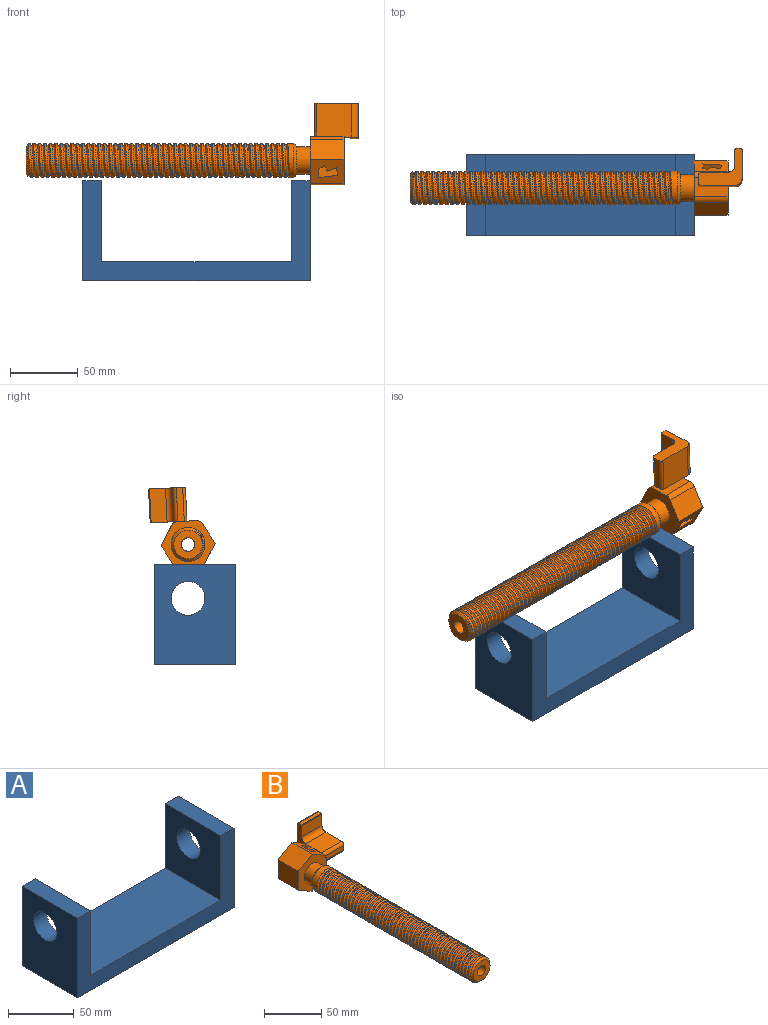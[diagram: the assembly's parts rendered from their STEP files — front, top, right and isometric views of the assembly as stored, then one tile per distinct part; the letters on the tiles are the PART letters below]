
ASSEMBLY  parts=2 mates=1
PART A: 12 faces, bbox 168x60x74 mm
  f0: plane 74x60mm, normal (-1,0,0), area 3949.1mm2, adj f1,f7,f8,f9,f10
  f1: plane 168x60mm, normal (0,0,-1), area 10080mm2, adj f0,f2,f8,f9
  f2: plane 74x60mm, normal (1,0,0), area 3949.1mm2, adj f1,f3,f8,f9,f11
  f3: plane 60x14mm, normal (0,0,1), area 840mm2, adj f2,f4,f8,f9
  f4: plane 60x60mm, normal (-1,0,0), area 3109.1mm2, adj f3,f5,f8,f9,f11
  f5: plane 140x60mm, normal (0,0,1), area 8400mm2, adj f4,f6,f8,f9
  f6: plane 60x60mm, normal (1,0,0), area 3109.1mm2, adj f5,f7,f8,f9,f10
  f7: plane 60x14mm, normal (0,0,1), area 840mm2, adj f0,f6,f8,f9
  f8: plane 168x74mm, normal (0,-1,0), area 4032mm2, adj f0,f1,f2,f3,f4,f5,f6,f7
  f9: plane 168x74mm, normal (0,1,0), area 4032mm2, adj f0,f1,f2,f3,f4,f5,f6,f7
  f10: cylinder r=12.5mm len=25mm, axis (1,0,0), area 1099.6mm2, adj f0,f6
  f11: cylinder r=12.5mm len=25mm, axis (1,0,0), area 1099.6mm2, adj f2,f4
PART B: 91 faces, bbox 60.5x247.5x48.1 mm
  f0: plane 25x14.23mm, normal (1,0,0), area 200.3mm2, adj f7,f8,f65,f66,f78,f79,f80,f81
  f1: plane 25x14.82mm, normal (0.5,0,0.87), area 340.3mm2, adj f4,f7,f8,f65,f71,f72,f73,f74
  f2: plane 25x17.32mm, normal (-0.5,0,-0.87), area 412.4mm2, adj f5,f6,f7,f8,f67,f68,f69,f70
  f3: cylinder r=5mm len=235mm, axis (0,1,0), area 7166mm2, adj f8,f58,f67,f68,f69,f70,f71,f72
  f4: plane 25x17.32mm, normal (-0.5,0,0.87), area 500mm2, adj f1,f5,f7,f8
  f5: plane 25x20mm, normal (-1,0,0), area 500mm2, adj f2,f4,f7,f8
  f6: plane 25x14.82mm, normal (0.5,0,-0.87), area 427.8mm2, adj f2,f7,f8,f66
  f7: plane 40x34.64mm, normal (0,-1,0), area 722.4mm2, adj f0,f1,f2,f4,f5,f6,f9,f65
  f8: plane 40x34.64mm, normal (0,1,0), area 958mm2, adj f0,f1,f2,f3,f4,f5,f6,f65
  f9: cylinder r=10mm len=20mm, axis (0,1,0), area 628.3mm2, adj f7,f59
  f10: cylinder r=12.5mm len=25mm, axis (0,1,0), area 462.9mm2, adj f57,f60,f62,f63,f64
  f11: cylinder r=12.5mm len=25mm, axis (0,1,0), area 100.8mm2, adj f12,f61,f63,f64
  f12: cylinder r=12.5mm len=25mm, axis (0,1,0), area 125.8mm2, adj f11,f13,f63,f64
  f13: cylinder r=12.5mm len=25mm, axis (0,1,0), area 125.7mm2, adj f12,f14,f63,f64
  f14: cylinder r=12.5mm len=25mm, axis (0,1,0), area 125.8mm2, adj f13,f15,f63,f64
  f15: cylinder r=12.5mm len=25mm, axis (0,1,0), area 125.6mm2, adj f14,f16,f63,f64
  f16: cylinder r=12.5mm len=25mm, axis (0,1,0), area 125.7mm2, adj f15,f17,f63,f64
  f17: cylinder r=12.5mm len=25mm, axis (0,1,0), area 125.7mm2, adj f16,f18,f63,f64
  f18: cylinder r=12.5mm len=25mm, axis (0,1,0), area 125.8mm2, adj f17,f19,f63,f64
  f19: cylinder r=12.5mm len=25mm, axis (0,1,0), area 125.7mm2, adj f18,f20,f63,f64
  f20: cylinder r=12.5mm len=25mm, axis (0,1,0), area 125.7mm2, adj f19,f21,f63,f64
  f21: cylinder r=12.5mm len=25mm, axis (0,1,0), area 125.7mm2, adj f20,f22,f63,f64
  f22: cylinder r=12.5mm len=25mm, axis (0,1,0), area 125.7mm2, adj f21,f23,f63,f64
  f23: cylinder r=12.5mm len=25mm, axis (0,1,0), area 125.8mm2, adj f22,f24,f63,f64
  f24: cylinder r=12.5mm len=25mm, axis (0,1,0), area 125.6mm2, adj f23,f25,f63,f64
  f25: cylinder r=12.5mm len=25mm, axis (0,1,0), area 125.7mm2, adj f24,f26,f63,f64
  f26: cylinder r=12.5mm len=25mm, axis (0,1,0), area 125.7mm2, adj f25,f27,f63,f64
  f27: cylinder r=12.5mm len=25mm, axis (0,1,0), area 125.8mm2, adj f26,f28,f63,f64
  f28: cylinder r=12.5mm len=25mm, axis (0,1,0), area 125.7mm2, adj f27,f29,f63,f64
  f29: cylinder r=12.5mm len=25mm, axis (0,1,0), area 125.7mm2, adj f28,f30,f63,f64
  f30: cylinder r=12.5mm len=25mm, axis (0,1,0), area 125.7mm2, adj f29,f31,f63,f64
  f31: cylinder r=12.5mm len=25mm, axis (0,1,0), area 125.7mm2, adj f30,f32,f63,f64
  f32: cylinder r=12.5mm len=25mm, axis (0,1,0), area 125.8mm2, adj f31,f33,f63,f64
  f33: cylinder r=12.5mm len=25mm, axis (0,1,0), area 125.7mm2, adj f32,f34,f63,f64
  f34: cylinder r=12.5mm len=25mm, axis (0,1,0), area 125.7mm2, adj f33,f35,f63,f64
  f35: cylinder r=12.5mm len=25mm, axis (0,1,0), area 125.7mm2, adj f34,f36,f63,f64
  f36: cylinder r=12.5mm len=25mm, axis (0,1,0), area 125.8mm2, adj f35,f37,f63,f64
  f37: cylinder r=12.5mm len=25mm, axis (0,1,0), area 125.7mm2, adj f36,f38,f63,f64
  f38: cylinder r=12.5mm len=25mm, axis (0,1,0), area 125.7mm2, adj f37,f39,f63,f64
  f39: cylinder r=12.5mm len=25mm, axis (0,1,0), area 125.7mm2, adj f38,f40,f63,f64
  f40: cylinder r=12.5mm len=25mm, axis (0,1,0), area 125.7mm2, adj f39,f41,f63,f64
  f41: cylinder r=12.5mm len=25mm, axis (0,1,0), area 125.8mm2, adj f40,f42,f63,f64
  f42: cylinder r=12.5mm len=25mm, axis (0,1,0), area 125.7mm2, adj f41,f43,f63,f64
  f43: cylinder r=12.5mm len=25mm, axis (0,1,0), area 125.7mm2, adj f42,f44,f63,f64
  f44: cylinder r=12.5mm len=25mm, axis (0,1,0), area 125.7mm2, adj f43,f45,f63,f64
  f45: cylinder r=12.5mm len=25mm, axis (0,1,0), area 125.8mm2, adj f44,f46,f63,f64
  f46: cylinder r=12.5mm len=25mm, axis (0,1,0), area 125.7mm2, adj f45,f47,f63,f64
  f47: cylinder r=12.5mm len=25mm, axis (0,1,0), area 125.7mm2, adj f46,f48,f63,f64
  f48: cylinder r=12.5mm len=25mm, axis (0,1,0), area 125.7mm2, adj f47,f49,f63,f64
  f49: cylinder r=12.5mm len=25mm, axis (0,1,0), area 125.7mm2, adj f48,f50,f63,f64
  f50: cylinder r=12.5mm len=25mm, axis (0,1,0), area 125.8mm2, adj f49,f51,f63,f64
  f51: cylinder r=12.5mm len=25mm, axis (0,1,0), area 125.7mm2, adj f50,f52,f63,f64
  f52: cylinder r=12.5mm len=25mm, axis (0,1,0), area 125.7mm2, adj f51,f53,f63,f64
  f53: cylinder r=12.5mm len=25mm, axis (0,1,0), area 125.7mm2, adj f52,f54,f63,f64
  f54: cylinder r=12.5mm len=25mm, axis (0,1,0), area 125.8mm2, adj f53,f55,f63,f64
  f55: cylinder r=12.5mm len=25mm, axis (0,1,0), area 125.8mm2, adj f54,f56,f63,f64
  f56: cylinder r=12.5mm len=25mm, axis (0,1,0), area 125.7mm2, adj f55,f57,f63,f64
  f57: cylinder r=12.5mm len=25mm, axis (0,1,0), area 125.7mm2, adj f10,f56,f63,f64
  f58: plane 21x21mm, normal (0,-1,0), area 267.8mm2, adj f3,f61
  f59: plane 21x21mm, normal (0,1,0), area 32.2mm2, adj f9,f60
  f60: cone r=12.5mm half-angle=45deg, axis (0,-1,0), area 204.4mm2, adj f10,f59
  f61: cone r=10.5mm half-angle=45deg, axis (0,1,0), area 155.5mm2, adj f11,f58,f63,f64
  f62: plane 2.4x1.54mm, normal (0,0,-1), area 1.8mm2, adj f10,f63,f64
  f63: bspline ~195.27x29.19mm, area 6874.5mm2, adj f10,f11,f12,f13,f14,f15,f16,f17
  f64: bspline ~195.35x29.19mm, area 6996.8mm2, adj f10,f11,f12,f13,f14,f15,f16,f17
  f65: cylinder r=5mm len=25mm, axis (0,1,0), area 130.9mm2, adj f0,f1,f7,f8,f77
  f66: cylinder r=5mm len=25mm, axis (0,1,0), area 130.9mm2, adj f0,f6,f7,f8
  f67: plane 14.26x11.18mm, normal (-0.7,0.58,0.41), area 69.5mm2, adj f2,f3,f68,f76
  f68: plane 13.83x12.19mm, normal (-0.35,-0.92,0.2), area 66.8mm2, adj f2,f3,f67,f69
  f69: plane 12.55x9.63mm, normal (-0.79,0.4,0.46), area 95mm2, adj f2,f3,f68,f70
  f70: plane 14.98x12.18mm, normal (-0.12,-0.99,0.07), area 81.1mm2, adj f2,f3,f69,f75
  f71: plane 15.75x9.75mm, normal (-0.7,0.58,0.41), area 69.5mm2, adj f1,f3,f72,f76
  f72: plane 16.15x10.61mm, normal (-0.35,-0.92,0.2), area 66.8mm2, adj f1,f3,f71,f73
  f73: plane 13.41x9.13mm, normal (-0.79,0.4,0.46), area 95mm2, adj f1,f3,f72,f74
  f74: plane 14.73x12.31mm, normal (-0.12,-0.99,0.07), area 81.1mm2, adj f1,f3,f73,f75
  f75: plane 30.95x18.96mm, normal (0.86,-0.13,-0.5), area 423mm2, adj f1,f2,f3,f70,f74,f76
  f76: plane 33.45x23.3mm, normal (0,1,0), area 183.4mm2, adj f1,f2,f3,f67,f71,f75
  f77: plane 32.28x27.24mm, normal (-1,0,0), area 246.2mm2, adj f8,f65,f78,f81,f82,f83,f84,f85
  f78: cylinder r=3mm len=25mm, axis (-1,0,0), area 117.8mm2, adj f0,f77,f79,f89,f90
  f79: plane 25x4.71mm, normal (0,-1,0), area 117.8mm2, adj f0,f78,f80,f90
  f80: cylinder r=2mm len=25mm, axis (-1,0,0), area 78.5mm2, adj f0,f79,f81,f90
  f81: plane 25.31x25mm, normal (0,0,-1), area 632.7mm2, adj f0,f77,f80,f82,f90
  f82: cylinder r=5mm len=25mm, axis (-1,0,0), area 196.3mm2, adj f77,f81,f83,f90
  f83: plane 25x21.53mm, normal (0,1,0), area 538.3mm2, adj f77,f82,f84,f90
  f84: cylinder r=0.71mm len=25mm, axis (-1,0,0), area 28mm2, adj f77,f83,f85,f90
  f85: plane 25x3.75mm, normal (0,0,1), area 93.8mm2, adj f77,f84,f86,f90
  f86: cylinder r=0.71mm len=25mm, axis (-1,0,0), area 28mm2, adj f77,f85,f87,f90
  f87: plane 25x11.82mm, normal (0,-1,0), area 295.4mm2, adj f77,f86,f88,f90
  f88: cylinder r=5mm len=25mm, axis (-1,0,0), area 196.3mm2, adj f77,f87,f89,f90
  f89: plane 25x19.13mm, normal (0,0,1), area 478.3mm2, adj f77,f78,f88,f90
  f90: plane 32.31x27.24mm, normal (1,0,0), area 401.6mm2, adj f78,f79,f80,f81,f82,f83,f84,f85
PLACE A t=(-17.62,13.63,0)mm fixed
PLACE B rot(axis=(-0.59,-0.59,-0.56),121.6deg) t=(91.38,-11.37,74.84)mm
MATE pin_slot B.f3 <-> A.f10  axis (-1,0,0) through (66.38,-11.37,74.84)mm
